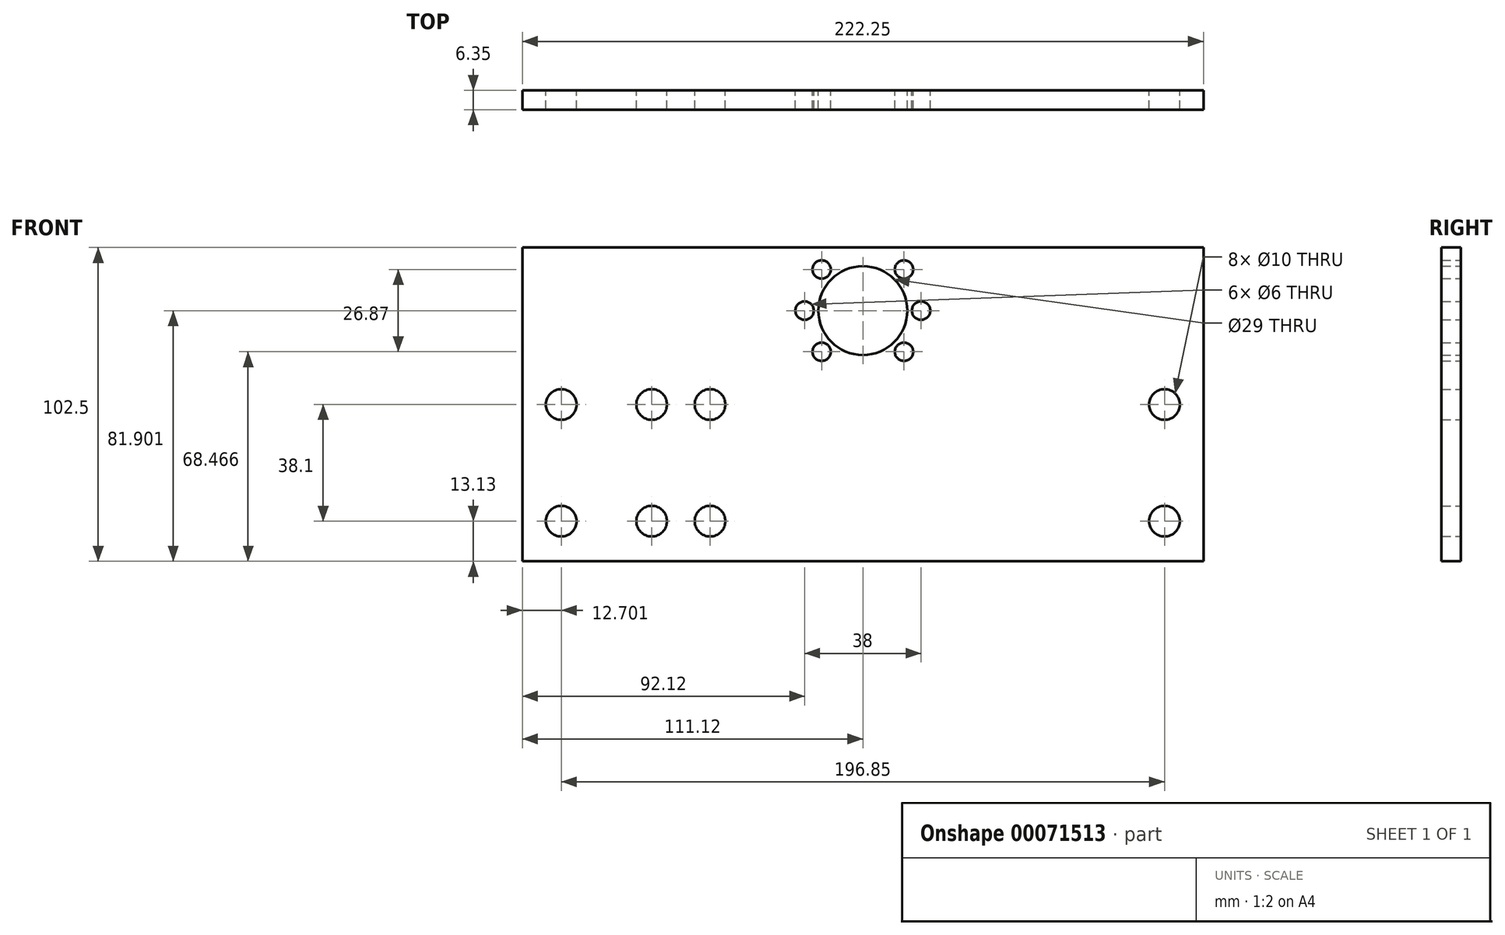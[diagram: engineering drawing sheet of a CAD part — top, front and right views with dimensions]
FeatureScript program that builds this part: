
annotation { "Feature Type Name" : "Feature", "Feature Type Description" : "" }
export const myFeature = defineFeature(function(context is Context, id is Id, definition is map)
    precondition{}
    {
        {
            var Q0;
            Q0=qCreatedBy(makeId("Front.planeOp"),FACE);
            var sketch = newSketch(context, id + "F0", { "sketchPlane" : qUnion([Q0])});
            skLineSegment(sketch, "E0.bottom", {"start": v(-107.3, 60.7) * mm, "end": v(114.94, 60.7) * mm});
            skLineSegment(sketch, "E0.top", {"start": v(-107.3, -41.8) * mm, "end": v(114.94, -41.8) * mm});
            skLineSegment(sketch, "E0.left", {"start": v(-107.3, 60.7) * mm, "end": v(-107.3, -41.8) * mm});
            skLineSegment(sketch, "E0.right", {"start": v(114.94, 60.7) * mm, "end": v(114.94, -41.8) * mm});
            skCircle(sketch, "E1", {"center": v(-94.6, 9.42) * mm, "radius": 5 * mm});
            skCircle(sketch, "E2", {"center": v(-94.6, -28.68) * mm, "radius": 5 * mm});
            skCircle(sketch, "E3", {"center": v(102.24, 9.42) * mm, "radius": 5 * mm});
            skCircle(sketch, "E4", {"center": v(102.24, -28.68) * mm, "radius": 5 * mm});
            skCircle(sketch, "E5", {"center": v(-65.1, 9.42) * mm, "radius": 5 * mm});
            skCircle(sketch, "E6.0.1.0", {"center": v(-65.1, -28.68) * mm, "radius": 5 * mm});
            skCircle(sketch, "E6.1.0.0", {"center": v(-46.04, 9.42) * mm, "radius": 5 * mm});
            skCircle(sketch, "E6.1.1.0", {"center": v(-46.04, -28.68) * mm, "radius": 5 * mm});
            skLineSegment(sketch, "E6.direction1", {"start": v(-65.1, 9.42) * mm, "end": v(-46.04, 9.42) * mm, "construction": true});
            skLineSegment(sketch, "E6.direction2", {"start": v(-65.1, 9.42) * mm, "end": v(-65.1, -28.68) * mm, "construction": true});
            skCircle(sketch, "E7", {"center": v(3.8, 40.1) * mm, "radius": 14.5 * mm});
            skCircle(sketch, "E8.1.0", {"center": v(-9.63, 53.53) * mm, "radius": 3 * mm});
            skCircle(sketch, "E8.2.0", {"center": v(-15.2, 40.1) * mm, "radius": 3 * mm});
            skCircle(sketch, "E8.3.0", {"center": v(-9.63, 26.66) * mm, "radius": 3 * mm});
            skCircle(sketch, "E8.5.0", {"center": v(17.24, 26.66) * mm, "radius": 3 * mm});
            skCircle(sketch, "E8.6.0", {"center": v(22.8, 40.1) * mm, "radius": 3 * mm});
            skCircle(sketch, "E8.7.0", {"center": v(17.24, 53.53) * mm, "radius": 3 * mm});
            skSolve(sketch);
        }
        {
            var Q0;
            Q0 = qSketchRegion(id + "F0", true);
            extrude(context, id + "F1", {"entities" : qUnion([Q0]), "depth" : 6.35 * mm});
        }
    });
